# Revit family: Rectangle
name_source: partatom
category: Furniture Systems
units: mm (PartAtom-declared; Revit-internal decimal feet)

## family parameters
Always vertical = Yes
Cut with Voids When Loaded = No
OmniClass Number = 23.40.00.00
OmniClass Title = Equipment and Furnishings
Part Type = Normal
Room Calculation Point = No
Round Connector Dimension = Use Diameter
Shared = No
Work Plane-Based = No

## types (3) — shared parameters
Assembly Code = E2020200
Manufacturer = Gresham Office Funiture
Range = SEATING
Seat = Gresham - Blue Fabric
URL = www.gof.co.uk

## per-type parameters (varying)
| type | Base Height | Castors | Glides | Legs | Model | Product Code |
| ES01 | 25 mm  [stored 0.082021 ft] | No | Yes | No |  |  |
| ES01C | 72 mm  [stored 0.23622 ft] | Yes | No | No | CUBE | ES01C |
| ES01M | 100 mm  [stored 0.328084 ft] | No | No | Yes | CUBE | ES01M |

note: [stored X ft] marks values corroborated as IEEE doubles in the binary element streams (Revit-internal decimal feet)

## geometry (parser evidence)
native form markers: Sweep x16
no freeform markers — native parametric forms only
